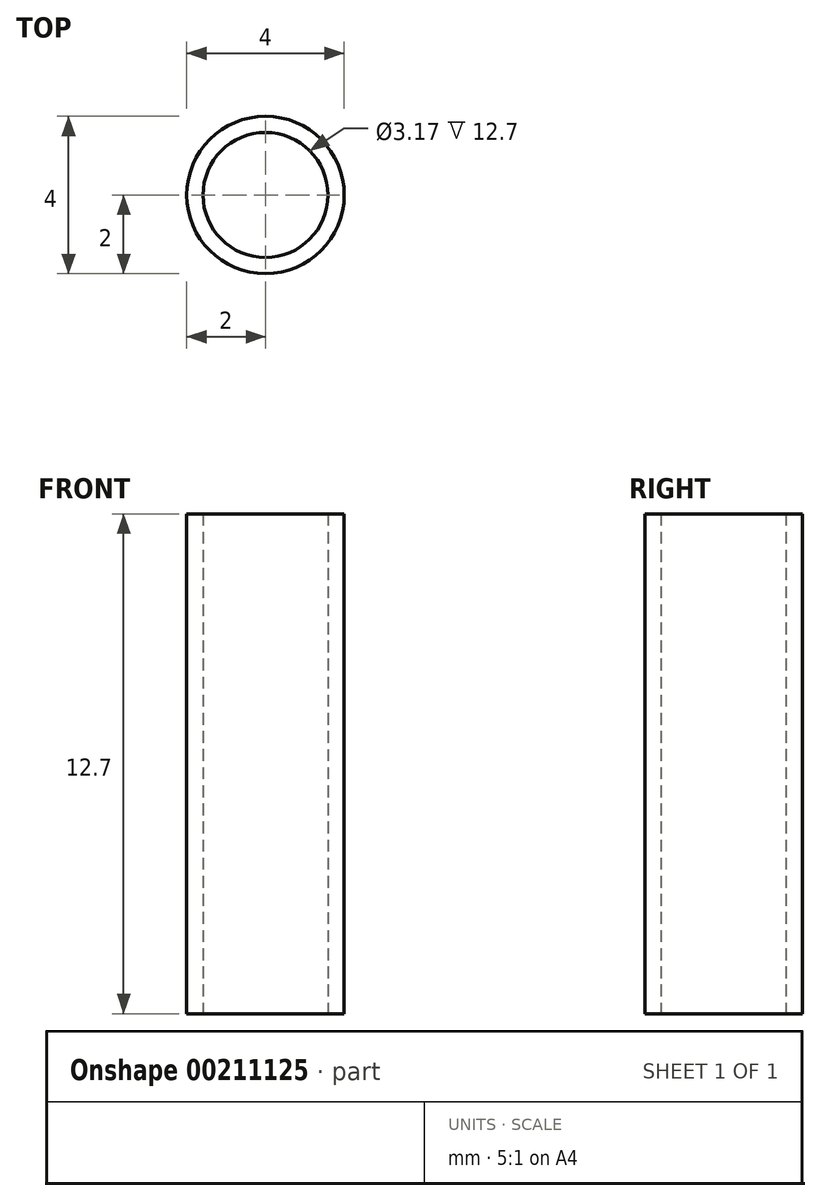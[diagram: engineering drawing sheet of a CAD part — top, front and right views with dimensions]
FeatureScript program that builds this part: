
annotation { "Feature Type Name" : "Feature", "Feature Type Description" : "" }
export const myFeature = defineFeature(function(context is Context, id is Id, definition is map)
    precondition{}
    {
        {
            var Q0;
            Q0=qCreatedBy(makeId("Top.planeOp"),FACE);
            var sketch = newSketch(context, id + "F0", { "sketchPlane" : qUnion([Q0])});
            skCircle(sketch, "E0", {"center": v(0, 0) * mm, "radius": 2 * mm});
            skCircle(sketch, "E1", {"center": v(0, 0) * mm, "radius": 1.59 * mm});
            skSolve(sketch);
        }
        {
            var Q0;
            Q0 = qSketchRegion(id + "F0", true);
            extrude(context, id + "F1", {"entities" : qUnion([Q0]), "depth" : 12.7 * mm});
        }
    });
